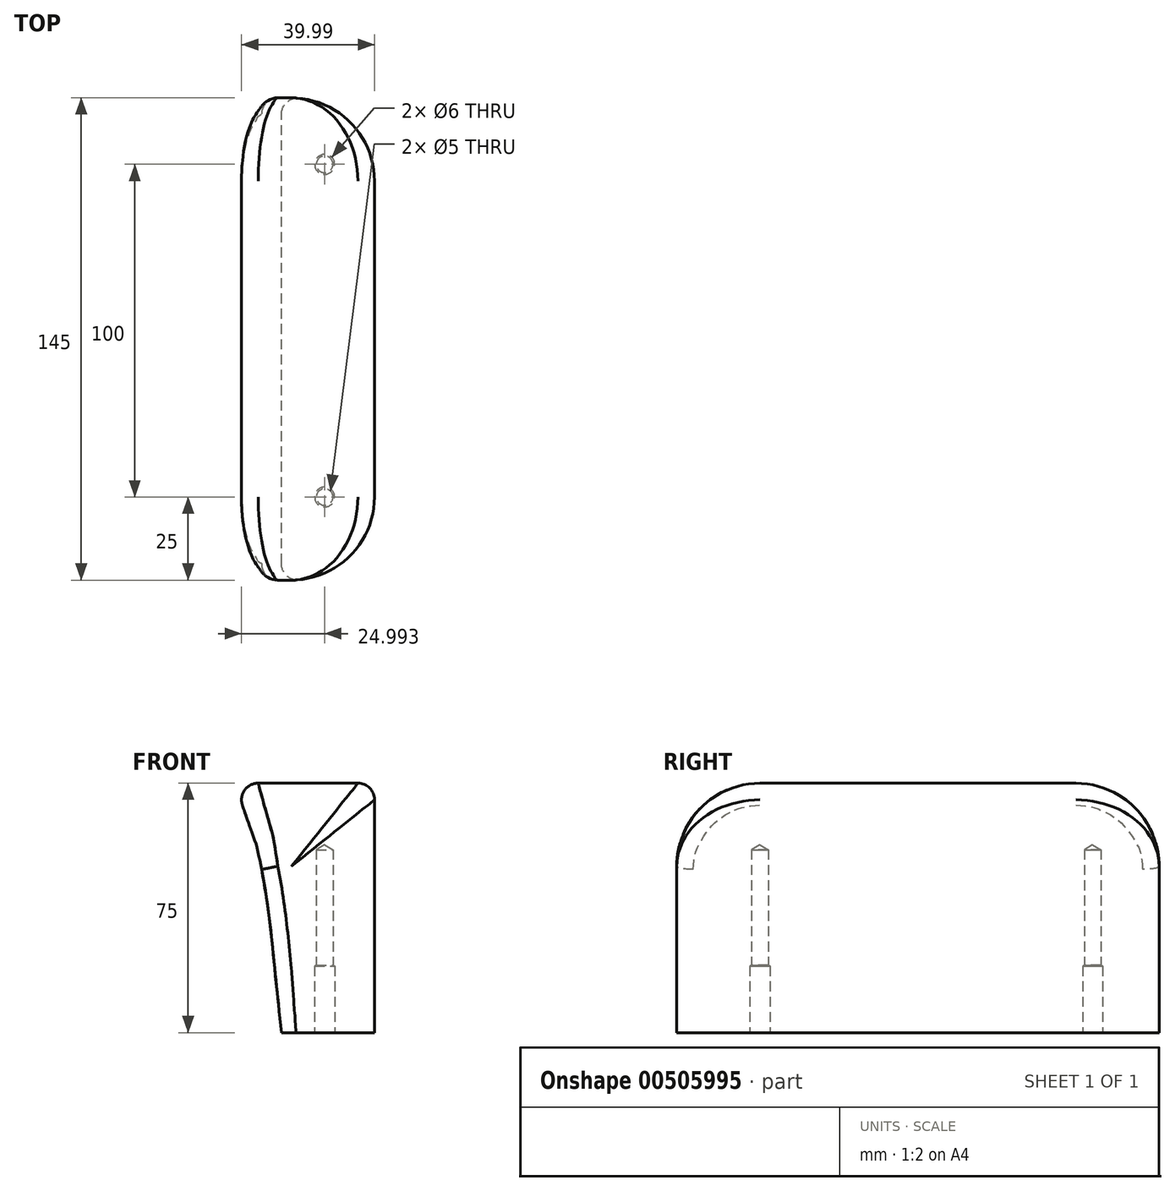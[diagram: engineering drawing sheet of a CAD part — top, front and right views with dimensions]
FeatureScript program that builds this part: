
annotation { "Feature Type Name" : "Feature", "Feature Type Description" : "" }
export const myFeature = defineFeature(function(context is Context, id is Id, definition is map)
    precondition{}
    {
        {
            var Q0;
            Q0=qCreatedBy(makeId("Front.planeOp"),FACE);
            var sketch = newSketch(context, id + "F0", { "sketchPlane" : qUnion([Q0])});
            skLineSegment(sketch, "E0", {"start": v(16.02, -55) * mm, "end": v(-11.98, -55) * mm});
            skLineSegment(sketch, "E1", {"start": v(-18.98, 20) * mm, "end": v(11.02, 20) * mm});
            skLineSegment(sketch, "E2", {"start": v(16.02, 15) * mm, "end": v(16.02, -55) * mm});
            skArc(sketch, "E3.filletArc", {"start": v(-18.98, 20) * mm, "mid": v(-22.99, 18) * mm, "end": v(-23.77, 13.57) * mm});
            skFitSpline(sketch, "E4", {"points": [v(-23.77, 13.57) * mm, v(-19.13, 0) * mm, v(-16.46, -14.53) * mm, v(-13.72, -38.54) * mm, v(-11.98, -55) * mm], "startDerivative": vector(61.03, -178.6) * mm, "endDerivative": vector(3.77, -41.32) * mm});
            skPoint(sketch, "E5.visualSharp", {"position": v(16.02, 20) * mm});
            skArc(sketch, "E5.filletArc", {"start": v(16.02, 15) * mm, "mid": v(14.56, 18.54) * mm, "end": v(11.02, 20) * mm});
            skSolve(sketch);
        }
        {
            var Q0;
            Q0=makeQuery(id+"F0.imprint","IMPRINT",FACE,{"disambiguationData":[TD([[makeQuery(id+"F0.imprint","IMPRINT",EDGE,{"derivedFrom":sQuery(id+"F0.wireOp",EDGE,"E0")}),-1.0]])]});
            extrude(context, id + "F1", {"entities" : qUnion([Q0]), "depth" : 145 * mm, "offsetDistance" : 25 * mm});
        }
        {
            var Q0;
            Q0=makeQuery(id+"F1.opExtrude","SWEPT_FACE",FACE,{"disambiguationData":[OSD([sQuery(id+"F0.wireOp",EDGE,"E0")])]});
            var sketch = newSketch(context, id + "F2", { "sketchPlane" : qUnion([Q0])});
            skPoint(sketch, "E6", {"position": v(1.02, 120) * mm});
            skPoint(sketch, "E7", {"position": v(1.02, 20) * mm});
            skSolve(sketch);
        }
        {
            var Q0;
            Q0=sQuery(id+"F2.wireOp",VERTEX,"E6");
            var Q1;
            Q1=sQuery(id+"F2.wireOp",VERTEX,"E7");
            var Q2;
            Q2=makeQuery(id+"F1.opExtrude","SWEPT_BODY",BODY,{"disambiguationData":[OSD([sQuery(id+"F0.wireOp",EDGE,"E0"),sQuery(id+"F0.wireOp",EDGE,"E1"),sQuery(id+"F0.wireOp",EDGE,"E2"),sQuery(id+"F0.wireOp",EDGE,"E3.filletArc"),sQuery(id+"F0.wireOp",EDGE,"E4"),sQuery(id+"F0.wireOp",EDGE,"E5.filletArc")])]});
            hole(context, id + "F3", {"style" : HoleStyle.SIMPLE, "endStyle" : HoleEndStyle.BLIND, "holeDiameter" : 5 * mm, "holeDepth" : 55 * mm, "isTappedThrough" : true, "tappedDepth" : 12 * mm, "tapClearance" : 3, "locations" : qUnion([Q0, Q1]), "scope" : qUnion([Q2]), "majorDiameter" : 5 * mm});
        }
        {
            var Q0;
            Q0=makeQuery(id+"F1.opExtrude","CAP_EDGE",EDGE,{"disambiguationData":[OSD([sQuery(id+"F0.wireOp",EDGE,"E1")])],"isStart":false});
            var Q1;
            Q1=makeQuery(id+"F1.opExtrude","CAP_EDGE",EDGE,{"disambiguationData":[OSD([sQuery(id+"F0.wireOp",EDGE,"E1")])],"isStart":true});
            fillet(context, id + "F4", {"entities" : qUnion([Q0, Q1]), "radius" : 25 * mm, "tangentPropagation" : true, "allowEdgeOverflow" : false});
        }
        {
            var Q0;
            Q0=makeQuery(id+"F4.opFillet","BLEND_EDGE",EDGE,{"blendedFrom":[makeQuery(id+"F1.opExtrude","CAP_EDGE",EDGE,{"disambiguationData":[OSD([sQuery(id+"F0.wireOp",EDGE,"E1")])],"isStart":false}),makeQuery(id+"F1.opExtrude","SWEPT_FACE",FACE,{"disambiguationData":[OSD([sQuery(id+"F0.wireOp",EDGE,"E4")])]})],"blendedInto":[makeQuery(id+"F1.opExtrude","SWEPT_FACE",FACE,{"disambiguationData":[OSD([sQuery(id+"F0.wireOp",EDGE,"E4")])]})]});
            var Q1;
            Q1=makeQuery(id+"F4.opFillet","BLEND_EDGE",EDGE,{"blendedFrom":[makeQuery(id+"F1.opExtrude","CAP_EDGE",EDGE,{"disambiguationData":[OSD([sQuery(id+"F0.wireOp",EDGE,"E1")])],"isStart":true}),makeQuery(id+"F1.opExtrude","SWEPT_FACE",FACE,{"disambiguationData":[OSD([sQuery(id+"F0.wireOp",EDGE,"E4")])]})],"blendedInto":[makeQuery(id+"F1.opExtrude","SWEPT_FACE",FACE,{"disambiguationData":[OSD([sQuery(id+"F0.wireOp",EDGE,"E4")])]})]});
            fillet(context, id + "F5", {"entities" : qUnion([Q0, Q1]), "radius" : 5 * mm, "tangentPropagation" : true, "allowEdgeOverflow" : false});
        }
        {
            var Q0;
            Q0=sQuery(id+"F2.wireOp",VERTEX,"E7");
            var Q1;
            Q1=sQuery(id+"F2.wireOp",VERTEX,"E6");
            var Q2;
            Q2=makeQuery(id+"F1.opExtrude","SWEPT_BODY",BODY,{"disambiguationData":[OSD([sQuery(id+"F0.wireOp",EDGE,"E0"),sQuery(id+"F0.wireOp",EDGE,"E1"),sQuery(id+"F0.wireOp",EDGE,"E2"),sQuery(id+"F0.wireOp",EDGE,"E3.filletArc"),sQuery(id+"F0.wireOp",EDGE,"E4"),sQuery(id+"F0.wireOp",EDGE,"E5.filletArc")])]});
            hole(context, id + "F6", {"style" : HoleStyle.SIMPLE, "endStyle" : HoleEndStyle.BLIND, "holeDiameter" : 6 * mm, "majorDiameter" : 5 * mm, "holeDepth" : 20 * mm, "isTappedThrough" : true, "tappedDepth" : 12 * mm, "tapClearance" : 3, "locations" : qUnion([Q0, Q1]), "scope" : qUnion([Q2])});
        }
    });
